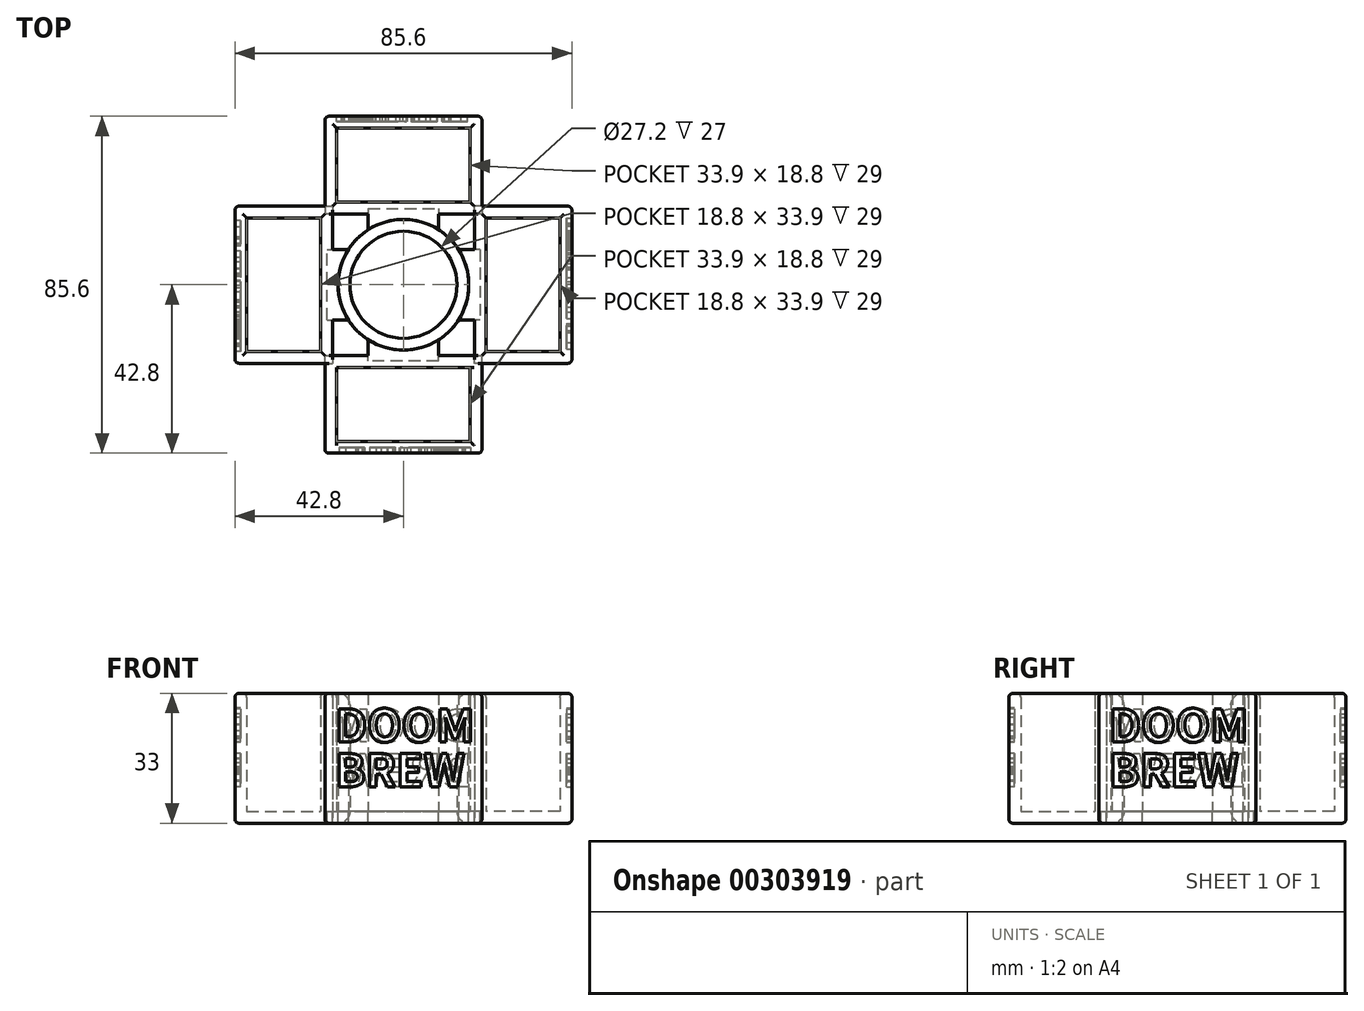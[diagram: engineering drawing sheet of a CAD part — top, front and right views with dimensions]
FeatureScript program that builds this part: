
annotation { "Feature Type Name" : "Feature", "Feature Type Description" : "" }
export const myFeature = defineFeature(function(context is Context, id is Id, definition is map)
    precondition{}
    {
        {
            var Q0;
            Q0=qCreatedBy(makeId("Top.planeOp"),FACE);
            var sketch = newSketch(context, id + "F0", { "sketchPlane" : qUnion([Q0])});
            skLineSegment(sketch, "E0.bottom", {"start": v(16.95, -9.4) * mm, "end": v(-16.95, -9.4) * mm});
            skLineSegment(sketch, "E0.top", {"start": v(16.95, 9.4) * mm, "end": v(-16.95, 9.4) * mm});
            skLineSegment(sketch, "E0.left", {"start": v(16.95, -9.4) * mm, "end": v(16.95, 9.4) * mm});
            skLineSegment(sketch, "E0.right", {"start": v(-16.95, -9.4) * mm, "end": v(-16.95, 9.4) * mm});
            skPoint(sketch, "E0.middle", {"position": v(0, 0) * mm});
            skLineSegment(sketch, "E1.0", {"start": v(19.95, 12.4) * mm, "end": v(-19.95, 12.4) * mm});
            skLineSegment(sketch, "E1.1", {"start": v(19.95, -12.4) * mm, "end": v(19.95, 12.4) * mm});
            skLineSegment(sketch, "E1.2", {"start": v(19.95, -12.4) * mm, "end": v(-19.95, -12.4) * mm});
            skLineSegment(sketch, "E1.3", {"start": v(-19.95, -12.4) * mm, "end": v(-19.95, 12.4) * mm});
            skLineSegment(sketch, "E2", {"start": v(0, 12.4) * mm, "end": v(0, 30.4) * mm, "construction": true});
            skCircle(sketch, "E3", {"center": v(0, 30.4) * mm, "radius": 13.6 * mm});
            skCircle(sketch, "E4.0", {"center": v(0, 30.4) * mm, "radius": 16.6 * mm});
            skLineSegment(sketch, "E5.bottom", {"start": v(8.92, 10.98) * mm, "end": v(-8.92, 10.98) * mm});
            skLineSegment(sketch, "E5.top", {"start": v(8.92, 16.62) * mm, "end": v(-8.92, 16.62) * mm});
            skLineSegment(sketch, "E5.left", {"start": v(8.92, 10.98) * mm, "end": v(8.92, 16.62) * mm});
            skLineSegment(sketch, "E5.right", {"start": v(-8.92, 10.98) * mm, "end": v(-8.92, 16.62) * mm});
            skPoint(sketch, "E5.middle", {"position": v(0, 13.8) * mm});
            skSolve(sketch);
        }
        {
            var Q0;
            Q0=makeQuery(id+"F0.imprint","IMPRINT",FACE,{"disambiguationData":[TD([[makeQuery(id+"F0.imprint","IMPRINT",EDGE,{"derivedFrom":sQuery(id+"F0.wireOp",EDGE,"E0.bottom")}),1.0]])]});
            var Q1;
            {var subQ0=sQuery(id+"F0.wireOp",EDGE,"E1.0");var subQ1=makeQuery(id+"F0.imprint","INTERSECT",VERTEX,{"derivedFrom":[subQ0,sQuery(id+"F0.wireOp",EDGE,"icXzgRXt-Ih2i-wxRq-pmOV-9hTM5KUKghl6")]});Q1=makeQuery(id+"F0.imprint","IMPRINT",FACE,{"disambiguationData":[TD([[makeQuery(id+"F0.imprint","IMPRINT",EDGE,{"disambiguationData":[TD([[subQ1,1.0]])],"derivedFrom":subQ0}),1.0]])]});}
            var Q2;
            {var subQ5=sQuery(id+"F0.wireOp",EDGE,"E5.bottom");Q2=makeQuery(id+"F0.imprint","IMPRINT",FACE,{"disambiguationData":[TD([[makeQuery(id+"F0.imprint","IMPRINT",EDGE,{"derivedFrom":subQ5}),-1.0]])]});}
            var Q3;
            {var subQ0=sQuery(id+"F0.wireOp",EDGE,"E5.left");var subQ1=sQuery(id+"F0.wireOp",EDGE,"E1.0");var subQ2=makeQuery(id+"F0.imprint","INTERSECT",VERTEX,{"derivedFrom":[subQ1,subQ0]});Q3=makeQuery(id+"F0.imprint","IMPRINT",FACE,{"disambiguationData":[TD([[makeQuery(id+"F0.imprint","IMPRINT",EDGE,{"disambiguationData":[TD([[subQ2,-1.0]])],"derivedFrom":subQ1}),-1.0]])]});}
            extrude(context, id + "F1", {"entities" : qUnion([Q0, Q1, Q2, Q3]), "depth" : 30 * mm});
        }
        {
            var Q0;
            Q0=makeQuery(id+"F0.imprint","IMPRINT",FACE,{"disambiguationData":[TD([[makeQuery(id+"F0.imprint","IMPRINT",EDGE,{"derivedFrom":sQuery(id+"F0.wireOp",EDGE,"E0.bottom")}),1.0]])]});
            var Q1;
            {var subQ0=sQuery(id+"F0.wireOp",EDGE,"Or8qQWFx-MEau-wVHM-B5Wl-hgzWRqUUP7mJ");Q1=makeQuery(id+"F0.imprint","IMPRINT",FACE,{"disambiguationData":[TD([[makeQuery(id+"F0.imprint","IMPRINT",EDGE,{"derivedFrom":subQ0}),-1.0]])]});}
            var Q2;
            {var subQ3=sQuery(id+"F0.wireOp",EDGE,"icXzgRXt-Ih2i-wxRq-pmOV-9hTM5KUKghl6");Q2=makeQuery(id+"F0.imprint","IMPRINT",FACE,{"disambiguationData":[TD([[makeQuery(id+"F0.imprint","IMPRINT",EDGE,{"derivedFrom":subQ3}),-1.0]])]});}
            var Q3;
            {var subQ0=sQuery(id+"F0.wireOp",EDGE,"E1.0");var subQ1=makeQuery(id+"F0.imprint","INTERSECT",VERTEX,{"derivedFrom":[subQ0,sQuery(id+"F0.wireOp",EDGE,"icXzgRXt-Ih2i-wxRq-pmOV-9hTM5KUKghl6")]});Q3=makeQuery(id+"F0.imprint","IMPRINT",FACE,{"disambiguationData":[TD([[makeQuery(id+"F0.imprint","IMPRINT",EDGE,{"disambiguationData":[TD([[subQ1,1.0]])],"derivedFrom":subQ0}),1.0]])]});}
            var Q4;
            {var subQ0=sQuery(id+"F0.wireOp",EDGE,"e3ElfhhZ-ileM-0cgF-CI4W-wu8BN25BOuYm");Q4=makeQuery(id+"F0.imprint","IMPRINT",FACE,{"disambiguationData":[TD([[makeQuery(id+"F0.imprint","IMPRINT",EDGE,{"derivedFrom":subQ0}),-1.0]])]});}
            var Q5;
            Q5=makeQuery(id+"F0.imprint","IMPRINT",FACE,{"disambiguationData":[TD([[makeQuery(id+"F0.imprint","IMPRINT",EDGE,{"derivedFrom":sQuery(id+"F0.wireOp",EDGE,"E0.bottom")}),-1.0]])]});
            extrude(context, id + "F2", {"entities" : qUnion([Q0, Q1, Q2, Q3, Q4, Q5]), "operationType" : NewBodyOperationType.ADD, "oppositeDirection" : true, "depth" : 3 * mm});
        }
        {
            var Q0;
            {var subQ0=sQuery(id+"F0.wireOp",EDGE,"E1.2");Q0=makeQuery(id+"F2.boolean.opBoolean","MERGE",FACE,{"derivedFrom":[makeQuery(id+"F1.opExtrude","SWEPT_FACE",FACE,{"disambiguationData":[OSD([subQ0])]}),makeQuery(id+"F2.opExtrude","SWEPT_FACE",FACE,{"disambiguationData":[OSD([subQ0])]})]});}
            var sketch = newSketch(context, id + "F3", { "sketchPlane" : qUnion([Q0])});
            skText(sketch, "E6", { "text": "DOOM\nBREW", "fontName": "NotoSansCJKsc-Bold.otf"});
            const initialGuessF3  = {"E6": [-0.01737, 0.01765, 1, 0, 0.0082]};
            skSetInitialGuess(sketch, initialGuessF3);
            skSolve(sketch);
        }
        {
            var Q0;
            Q0=qSketchRegion(id+"F3",true);
            extrude(context, id + "F4", {"entities" : qUnion([Q0]), "operationType" : NewBodyOperationType.REMOVE, "oppositeDirection" : true, "depth" : 1 * mm});
        }
        {
            var Q0;
            Q0=qSketchRegion(id+"F3",true);
            extrude(context, id + "F5", {"entities" : qUnion([Q0]), "operationType" : NewBodyOperationType.REMOVE, "oppositeDirection" : true, "depth" : 1.4 * mm});
        }
        {
            var Q0;
            Q0=makeQuery(id+"F1.opExtrude","SWEPT_BODY",BODY,{"disambiguationData":[OSD([sQuery(id+"F0.wireOp",EDGE,"E0.bottom"),sQuery(id+"F0.wireOp",EDGE,"E0.top"),sQuery(id+"F0.wireOp",EDGE,"E0.left"),sQuery(id+"F0.wireOp",EDGE,"E0.right"),sQuery(id+"F0.wireOp",EDGE,"E1.0"),sQuery(id+"F0.wireOp",EDGE,"E1.1"),sQuery(id+"F0.wireOp",EDGE,"E1.2"),sQuery(id+"F0.wireOp",EDGE,"E1.3")])]});
            var Q1;
            Q1=sQuery(id+"F0.wireOp",EDGE,"E3");
            circularPattern(context, id + "F6", {"entities" : qUnion([Q0]), "axis" : qUnion([Q1]), "angle" : 360 * degree, "instanceCount" : 4, "equalSpace" : true});
        }
        {
            var Q0;
            Q0=makeQuery(id+"F0.imprint","IMPRINT",FACE,{"disambiguationData":[TD([[makeQuery(id+"F0.imprint","IMPRINT",EDGE,{"derivedFrom":sQuery(id+"F0.wireOp",EDGE,"E3")}),-1.0]])]});
            var Q1;
            {var subQ5=sQuery(id+"F0.wireOp",EDGE,"E5.top");Q1=makeQuery(id+"F0.imprint","IMPRINT",FACE,{"disambiguationData":[TD([[makeQuery(id+"F0.imprint","IMPRINT",EDGE,{"derivedFrom":subQ5}),1.0]])]});}
            extrude(context, id + "F7", {"entities" : qUnion([Q0, Q1]), "depth" : 30 * mm});
        }
        {
            var Q0;
            Q0=makeQuery(id+"F6.opPattern","COPY",FACE,{"derivedFrom":makeQuery(id+"F1.opExtrude","CAP_FACE",FACE,{"disambiguationData":[OSD([sQuery(id+"F0.wireOp",EDGE,"E0.bottom"),sQuery(id+"F0.wireOp",EDGE,"E0.top"),sQuery(id+"F0.wireOp",EDGE,"E0.left"),sQuery(id+"F0.wireOp",EDGE,"E0.right"),sQuery(id+"F0.wireOp",EDGE,"E1.0"),sQuery(id+"F0.wireOp",EDGE,"E1.1"),sQuery(id+"F0.wireOp",EDGE,"E1.2"),sQuery(id+"F0.wireOp",EDGE,"E1.3"),sQuery(id+"F0.wireOp",EDGE,"E4.0"),sQuery(id+"F0.wireOp",EDGE,"E5.left"),sQuery(id+"F0.wireOp",EDGE,"E5.right")])],"isStart":true}),"instanceName":"3"});
            var Q1;
            Q1=makeQuery(id+"F6.opPattern","COPY",FACE,{"derivedFrom":makeQuery(id+"F1.opExtrude","CAP_FACE",FACE,{"disambiguationData":[OSD([sQuery(id+"F0.wireOp",EDGE,"E0.bottom"),sQuery(id+"F0.wireOp",EDGE,"E0.top"),sQuery(id+"F0.wireOp",EDGE,"E0.left"),sQuery(id+"F0.wireOp",EDGE,"E0.right"),sQuery(id+"F0.wireOp",EDGE,"E1.0"),sQuery(id+"F0.wireOp",EDGE,"E1.1"),sQuery(id+"F0.wireOp",EDGE,"E1.2"),sQuery(id+"F0.wireOp",EDGE,"E1.3"),sQuery(id+"F0.wireOp",EDGE,"E4.0"),sQuery(id+"F0.wireOp",EDGE,"E5.left"),sQuery(id+"F0.wireOp",EDGE,"E5.right")])],"isStart":true}),"instanceName":"2"});
            var Q2;
            Q2=makeQuery(id+"F0.imprint","IMPRINT",FACE,{"disambiguationData":[TD([[makeQuery(id+"F0.imprint","IMPRINT",EDGE,{"derivedFrom":sQuery(id+"F0.wireOp",EDGE,"E3")}),-1.0]])]});
            var Q3;
            Q3=makeQuery(id+"F6.opPattern","COPY",FACE,{"derivedFrom":makeQuery(id+"F1.opExtrude","CAP_FACE",FACE,{"disambiguationData":[OSD([sQuery(id+"F0.wireOp",EDGE,"E0.bottom"),sQuery(id+"F0.wireOp",EDGE,"E0.top"),sQuery(id+"F0.wireOp",EDGE,"E0.left"),sQuery(id+"F0.wireOp",EDGE,"E0.right"),sQuery(id+"F0.wireOp",EDGE,"E1.0"),sQuery(id+"F0.wireOp",EDGE,"E1.1"),sQuery(id+"F0.wireOp",EDGE,"E1.2"),sQuery(id+"F0.wireOp",EDGE,"E1.3"),sQuery(id+"F0.wireOp",EDGE,"E4.0"),sQuery(id+"F0.wireOp",EDGE,"E5.left"),sQuery(id+"F0.wireOp",EDGE,"E5.right")])],"isStart":true}),"instanceName":"1"});
            var Q4;
            {var subQ0=sQuery(id+"F0.wireOp",EDGE,"E5.left");var subQ1=sQuery(id+"F0.wireOp",EDGE,"E1.0");var subQ2=makeQuery(id+"F0.imprint","INTERSECT",VERTEX,{"derivedFrom":[subQ1,subQ0]});Q4=makeQuery(id+"F0.imprint","IMPRINT",FACE,{"disambiguationData":[TD([[makeQuery(id+"F0.imprint","IMPRINT",EDGE,{"disambiguationData":[TD([[subQ2,-1.0]])],"derivedFrom":subQ1}),-1.0]])]});}
            var Q5;
            {var subQ5=sQuery(id+"F0.wireOp",EDGE,"E5.bottom");Q5=makeQuery(id+"F0.imprint","IMPRINT",FACE,{"disambiguationData":[TD([[makeQuery(id+"F0.imprint","IMPRINT",EDGE,{"derivedFrom":subQ5}),-1.0]])]});}
            var Q6;
            {var subQ5=sQuery(id+"F0.wireOp",EDGE,"E5.top");Q6=makeQuery(id+"F0.imprint","IMPRINT",FACE,{"disambiguationData":[TD([[makeQuery(id+"F0.imprint","IMPRINT",EDGE,{"derivedFrom":subQ5}),1.0]])]});}
            extrude(context, id + "F8", {"entities" : qUnion([Q0, Q1, Q2, Q3, Q4, Q5, Q6]), "depth" : 3 * mm});
        }
        {
            var Q0;
            Q0=makeQuery(id+"F1.opExtrude","CAP_EDGE",EDGE,{"disambiguationData":[OSD([sQuery(id+"F0.wireOp",EDGE,"E0.bottom")])],"isStart":false});
            var Q1;
            Q1=makeQuery(id+"F1.opExtrude","CAP_EDGE",EDGE,{"disambiguationData":[OSD([sQuery(id+"F0.wireOp",EDGE,"E0.left")])],"isStart":false});
            var Q2;
            Q2=makeQuery(id+"F6.opPattern","COPY",EDGE,{"derivedFrom":makeQuery(id+"F1.opExtrude","CAP_EDGE",EDGE,{"disambiguationData":[OSD([sQuery(id+"F0.wireOp",EDGE,"E0.right")])],"isStart":false}),"instanceName":"1"});
            var Q3;
            Q3=makeQuery(id+"F6.opPattern","COPY",EDGE,{"derivedFrom":makeQuery(id+"F1.opExtrude","CAP_EDGE",EDGE,{"disambiguationData":[OSD([sQuery(id+"F0.wireOp",EDGE,"E0.bottom")])],"isStart":false}),"instanceName":"1"});
            var Q4;
            Q4=makeQuery(id+"F6.opPattern","COPY",EDGE,{"derivedFrom":makeQuery(id+"F1.opExtrude","CAP_EDGE",EDGE,{"disambiguationData":[OSD([sQuery(id+"F0.wireOp",EDGE,"E0.left")])],"isStart":false}),"instanceName":"1"});
            var Q5;
            Q5=makeQuery(id+"F6.opPattern","COPY",EDGE,{"derivedFrom":makeQuery(id+"F1.opExtrude","CAP_EDGE",EDGE,{"disambiguationData":[OSD([sQuery(id+"F0.wireOp",EDGE,"E0.top")])],"isStart":false}),"instanceName":"1"});
            var Q6;
            Q6=makeQuery(id+"F6.opPattern","COPY",EDGE,{"derivedFrom":makeQuery(id+"F1.opExtrude","CAP_EDGE",EDGE,{"disambiguationData":[OSD([sQuery(id+"F0.wireOp",EDGE,"E0.top")])],"isStart":false}),"instanceName":"3"});
            var Q7;
            Q7=makeQuery(id+"F6.opPattern","COPY",EDGE,{"derivedFrom":makeQuery(id+"F1.opExtrude","CAP_EDGE",EDGE,{"disambiguationData":[OSD([sQuery(id+"F0.wireOp",EDGE,"E0.left")])],"isStart":false}),"instanceName":"3"});
            var Q8;
            Q8=makeQuery(id+"F6.opPattern","COPY",EDGE,{"derivedFrom":makeQuery(id+"F1.opExtrude","CAP_EDGE",EDGE,{"disambiguationData":[OSD([sQuery(id+"F0.wireOp",EDGE,"E1.1")])],"isStart":false}),"instanceName":"3"});
            var Q9;
            Q9=makeQuery(id+"F1.opExtrude","CAP_EDGE",EDGE,{"disambiguationData":[OSD([sQuery(id+"F0.wireOp",EDGE,"E1.3")])],"isStart":false});
            var Q10;
            Q10=makeQuery(id+"F1.opExtrude","CAP_EDGE",EDGE,{"disambiguationData":[OSD([sQuery(id+"F0.wireOp",EDGE,"E1.2")])],"isStart":false});
            var Q11;
            Q11=makeQuery(id+"F1.opExtrude","CAP_EDGE",EDGE,{"disambiguationData":[OSD([sQuery(id+"F0.wireOp",EDGE,"E1.1")])],"isStart":false});
            var Q12;
            Q12=makeQuery(id+"F6.opPattern","COPY",EDGE,{"derivedFrom":makeQuery(id+"F1.opExtrude","CAP_EDGE",EDGE,{"disambiguationData":[OSD([sQuery(id+"F0.wireOp",EDGE,"E0.bottom")])],"isStart":false}),"instanceName":"3"});
            var Q13;
            Q13=makeQuery(id+"F6.opPattern","COPY",EDGE,{"derivedFrom":makeQuery(id+"F1.opExtrude","CAP_EDGE",EDGE,{"disambiguationData":[OSD([sQuery(id+"F0.wireOp",EDGE,"E0.right")])],"isStart":false}),"instanceName":"3"});
            var Q14;
            Q14=makeQuery(id+"F6.opPattern","COPY",EDGE,{"derivedFrom":makeQuery(id+"F1.opExtrude","CAP_EDGE",EDGE,{"disambiguationData":[OSD([sQuery(id+"F0.wireOp",EDGE,"E1.3")])],"isStart":false}),"instanceName":"3"});
            var Q15;
            Q15=makeQuery(id+"F6.opPattern","COPY",EDGE,{"derivedFrom":makeQuery(id+"F1.opExtrude","CAP_EDGE",EDGE,{"disambiguationData":[OSD([sQuery(id+"F0.wireOp",EDGE,"E1.2")])],"isStart":false}),"instanceName":"3"});
            var Q16;
            Q16=makeQuery(id+"F6.opPattern","COPY",EDGE,{"derivedFrom":makeQuery(id+"F1.opExtrude","CAP_EDGE",EDGE,{"disambiguationData":[OSD([sQuery(id+"F0.wireOp",EDGE,"E0.left")])],"isStart":false}),"instanceName":"2"});
            var Q17;
            Q17=makeQuery(id+"F6.opPattern","COPY",EDGE,{"derivedFrom":makeQuery(id+"F1.opExtrude","CAP_EDGE",EDGE,{"disambiguationData":[OSD([sQuery(id+"F0.wireOp",EDGE,"E1.1")])],"isStart":false}),"instanceName":"2"});
            var Q18;
            Q18=makeQuery(id+"F6.opPattern","COPY",EDGE,{"derivedFrom":makeQuery(id+"F1.opExtrude","CAP_EDGE",EDGE,{"disambiguationData":[OSD([sQuery(id+"F0.wireOp",EDGE,"E1.2")])],"isStart":false}),"instanceName":"2"});
            var Q19;
            Q19=makeQuery(id+"F6.opPattern","COPY",EDGE,{"derivedFrom":makeQuery(id+"F1.opExtrude","CAP_EDGE",EDGE,{"disambiguationData":[OSD([sQuery(id+"F0.wireOp",EDGE,"E0.bottom")])],"isStart":false}),"instanceName":"2"});
            var Q20;
            Q20=makeQuery(id+"F6.opPattern","COPY",EDGE,{"derivedFrom":makeQuery(id+"F1.opExtrude","CAP_EDGE",EDGE,{"disambiguationData":[OSD([sQuery(id+"F0.wireOp",EDGE,"E0.top")])],"isStart":false}),"instanceName":"2"});
            var Q21;
            Q21=makeQuery(id+"F6.opPattern","COPY",EDGE,{"derivedFrom":makeQuery(id+"F1.opExtrude","CAP_EDGE",EDGE,{"disambiguationData":[OSD([sQuery(id+"F0.wireOp",EDGE,"E0.right")])],"isStart":false}),"instanceName":"2"});
            var Q22;
            Q22=makeQuery(id+"F6.opPattern","COPY",EDGE,{"derivedFrom":makeQuery(id+"F1.opExtrude","CAP_EDGE",EDGE,{"disambiguationData":[OSD([sQuery(id+"F0.wireOp",EDGE,"E1.3")])],"isStart":false}),"instanceName":"2"});
            var Q23;
            Q23=makeQuery(id+"F6.opPattern","COPY",EDGE,{"derivedFrom":makeQuery(id+"F1.opExtrude","CAP_EDGE",EDGE,{"disambiguationData":[OSD([sQuery(id+"F0.wireOp",EDGE,"E1.1")])],"isStart":false}),"instanceName":"1"});
            var Q24;
            Q24=makeQuery(id+"F6.opPattern","COPY",EDGE,{"derivedFrom":makeQuery(id+"F1.opExtrude","CAP_EDGE",EDGE,{"disambiguationData":[OSD([sQuery(id+"F0.wireOp",EDGE,"E1.2")])],"isStart":false}),"instanceName":"1"});
            var Q25;
            {var subQ0=sQuery(id+"F0.wireOp",EDGE,"E1.2");var subQ1=sQuery(id+"F0.wireOp",EDGE,"E1.1");Q25=makeQuery(id+"F6.opPattern","COPY",EDGE,{"derivedFrom":makeQuery(id+"F2.boolean.opBoolean","MERGE",EDGE,{"derivedFrom":[makeQuery(id+"F1.opExtrude","SWEPT_EDGE",EDGE,{"disambiguationData":[OSD([subQ1,subQ0])]}),makeQuery(id+"F2.opExtrude","SWEPT_EDGE",EDGE,{"disambiguationData":[OSD([subQ1,subQ0])]})]}),"instanceName":"1"});}
            var Q26;
            {var subQ0=sQuery(id+"F0.wireOp",EDGE,"E1.3");var subQ1=sQuery(id+"F0.wireOp",EDGE,"E1.2");Q26=makeQuery(id+"F6.opPattern","COPY",EDGE,{"derivedFrom":makeQuery(id+"F2.boolean.opBoolean","MERGE",EDGE,{"derivedFrom":[makeQuery(id+"F1.opExtrude","SWEPT_EDGE",EDGE,{"disambiguationData":[OSD([subQ1,subQ0])]}),makeQuery(id+"F2.opExtrude","SWEPT_EDGE",EDGE,{"disambiguationData":[OSD([subQ1,subQ0])]})]}),"instanceName":"2"});}
            var Q27;
            {var subQ0=sQuery(id+"F0.wireOp",EDGE,"E1.2");var subQ1=sQuery(id+"F0.wireOp",EDGE,"E1.1");Q27=makeQuery(id+"F6.opPattern","COPY",EDGE,{"derivedFrom":makeQuery(id+"F2.boolean.opBoolean","MERGE",EDGE,{"derivedFrom":[makeQuery(id+"F1.opExtrude","SWEPT_EDGE",EDGE,{"disambiguationData":[OSD([subQ1,subQ0])]}),makeQuery(id+"F2.opExtrude","SWEPT_EDGE",EDGE,{"disambiguationData":[OSD([subQ1,subQ0])]})]}),"instanceName":"2"});}
            var Q28;
            {var subQ0=sQuery(id+"F0.wireOp",EDGE,"E1.3");var subQ1=sQuery(id+"F0.wireOp",EDGE,"E1.2");Q28=makeQuery(id+"F6.opPattern","COPY",EDGE,{"derivedFrom":makeQuery(id+"F2.boolean.opBoolean","MERGE",EDGE,{"derivedFrom":[makeQuery(id+"F1.opExtrude","SWEPT_EDGE",EDGE,{"disambiguationData":[OSD([subQ1,subQ0])]}),makeQuery(id+"F2.opExtrude","SWEPT_EDGE",EDGE,{"disambiguationData":[OSD([subQ1,subQ0])]})]}),"instanceName":"3"});}
            var Q29;
            {var subQ0=sQuery(id+"F0.wireOp",EDGE,"E1.2");var subQ1=sQuery(id+"F0.wireOp",EDGE,"E1.1");Q29=makeQuery(id+"F6.opPattern","COPY",EDGE,{"derivedFrom":makeQuery(id+"F2.boolean.opBoolean","MERGE",EDGE,{"derivedFrom":[makeQuery(id+"F1.opExtrude","SWEPT_EDGE",EDGE,{"disambiguationData":[OSD([subQ1,subQ0])]}),makeQuery(id+"F2.opExtrude","SWEPT_EDGE",EDGE,{"disambiguationData":[OSD([subQ1,subQ0])]})]}),"instanceName":"3"});}
            var Q30;
            {var subQ0=sQuery(id+"F0.wireOp",EDGE,"E1.3");var subQ1=sQuery(id+"F0.wireOp",EDGE,"E1.2");Q30=makeQuery(id+"F2.boolean.opBoolean","MERGE",EDGE,{"derivedFrom":[makeQuery(id+"F1.opExtrude","SWEPT_EDGE",EDGE,{"disambiguationData":[OSD([subQ1,subQ0])]}),makeQuery(id+"F2.opExtrude","SWEPT_EDGE",EDGE,{"disambiguationData":[OSD([subQ1,subQ0])]})]});}
            var Q31;
            {var subQ0=sQuery(id+"F0.wireOp",EDGE,"E1.2");var subQ1=sQuery(id+"F0.wireOp",EDGE,"E1.1");Q31=makeQuery(id+"F2.boolean.opBoolean","MERGE",EDGE,{"derivedFrom":[makeQuery(id+"F1.opExtrude","SWEPT_EDGE",EDGE,{"disambiguationData":[OSD([subQ1,subQ0])]}),makeQuery(id+"F2.opExtrude","SWEPT_EDGE",EDGE,{"disambiguationData":[OSD([subQ1,subQ0])]})]});}
            var Q32;
            {var subQ0=sQuery(id+"F0.wireOp",EDGE,"E1.3");var subQ1=sQuery(id+"F0.wireOp",EDGE,"E1.2");Q32=makeQuery(id+"F6.opPattern","COPY",EDGE,{"derivedFrom":makeQuery(id+"F2.boolean.opBoolean","MERGE",EDGE,{"derivedFrom":[makeQuery(id+"F1.opExtrude","SWEPT_EDGE",EDGE,{"disambiguationData":[OSD([subQ1,subQ0])]}),makeQuery(id+"F2.opExtrude","SWEPT_EDGE",EDGE,{"disambiguationData":[OSD([subQ1,subQ0])]})]}),"instanceName":"1"});}
            var Q33;
            Q33=makeQuery(id+"F6.opPattern","COPY",EDGE,{"derivedFrom":makeQuery(id+"F1.opExtrude","CAP_EDGE",EDGE,{"disambiguationData":[OSD([sQuery(id+"F0.wireOp",EDGE,"E1.3")])],"isStart":false}),"instanceName":"1"});
            var Q34;
            Q34=makeQuery(id+"F2.opExtrude","CAP_EDGE",EDGE,{"disambiguationData":[OSD([sQuery(id+"F0.wireOp",EDGE,"E1.2")])],"isStart":false});
            var Q35;
            Q35=makeQuery(id+"F6.opPattern","COPY",EDGE,{"derivedFrom":makeQuery(id+"F2.opExtrude","CAP_EDGE",EDGE,{"disambiguationData":[OSD([sQuery(id+"F0.wireOp",EDGE,"E1.2")])],"isStart":false}),"instanceName":"1"});
            var Q36;
            Q36=makeQuery(id+"F6.opPattern","COPY",EDGE,{"derivedFrom":makeQuery(id+"F2.opExtrude","CAP_EDGE",EDGE,{"disambiguationData":[OSD([sQuery(id+"F0.wireOp",EDGE,"E1.3")])],"isStart":false}),"instanceName":"1"});
            var Q37;
            Q37=makeQuery(id+"F2.opExtrude","CAP_EDGE",EDGE,{"disambiguationData":[OSD([sQuery(id+"F0.wireOp",EDGE,"E1.1")])],"isStart":false});
            var Q38;
            Q38=makeQuery(id+"F2.opExtrude","CAP_EDGE",EDGE,{"disambiguationData":[OSD([sQuery(id+"F0.wireOp",EDGE,"E1.3")])],"isStart":false});
            var Q39;
            Q39=makeQuery(id+"F6.opPattern","COPY",EDGE,{"derivedFrom":makeQuery(id+"F2.opExtrude","CAP_EDGE",EDGE,{"disambiguationData":[OSD([sQuery(id+"F0.wireOp",EDGE,"E1.1")])],"isStart":false}),"instanceName":"3"});
            var Q40;
            Q40=makeQuery(id+"F6.opPattern","COPY",EDGE,{"derivedFrom":makeQuery(id+"F2.opExtrude","CAP_EDGE",EDGE,{"disambiguationData":[OSD([sQuery(id+"F0.wireOp",EDGE,"E1.2")])],"isStart":false}),"instanceName":"3"});
            var Q41;
            Q41=makeQuery(id+"F6.opPattern","COPY",EDGE,{"derivedFrom":makeQuery(id+"F2.opExtrude","CAP_EDGE",EDGE,{"disambiguationData":[OSD([sQuery(id+"F0.wireOp",EDGE,"E1.1")])],"isStart":false}),"instanceName":"2"});
            var Q42;
            Q42=makeQuery(id+"F6.opPattern","COPY",EDGE,{"derivedFrom":makeQuery(id+"F2.opExtrude","CAP_EDGE",EDGE,{"disambiguationData":[OSD([sQuery(id+"F0.wireOp",EDGE,"E1.3")])],"isStart":false}),"instanceName":"3"});
            var Q43;
            Q43=makeQuery(id+"F6.opPattern","COPY",EDGE,{"derivedFrom":makeQuery(id+"F2.opExtrude","CAP_EDGE",EDGE,{"disambiguationData":[OSD([sQuery(id+"F0.wireOp",EDGE,"E1.1")])],"isStart":false}),"instanceName":"1"});
            var Q44;
            Q44=makeQuery(id+"F6.opPattern","COPY",EDGE,{"derivedFrom":makeQuery(id+"F2.opExtrude","CAP_EDGE",EDGE,{"disambiguationData":[OSD([sQuery(id+"F0.wireOp",EDGE,"E1.3")])],"isStart":false}),"instanceName":"2"});
            var Q45;
            Q45=makeQuery(id+"F6.opPattern","COPY",EDGE,{"derivedFrom":makeQuery(id+"F2.opExtrude","CAP_EDGE",EDGE,{"disambiguationData":[OSD([sQuery(id+"F0.wireOp",EDGE,"E1.2")])],"isStart":false}),"instanceName":"2"});
            fillet(context, id + "F9", {"entities" : qUnion([Q0, Q1, Q2, Q3, Q4, Q5, Q6, Q7, Q8, Q9, Q10, Q11, Q12, Q13, Q14, Q15, Q16, Q17, Q18, Q19, Q20, Q21, Q22, Q23, Q24, Q25, Q26, Q27, Q28, Q29, Q30, Q31, Q32, Q33, Q34, Q35, Q36, Q37, Q38, Q39, Q40, Q41, Q42, Q43, Q44, Q45]), "radius" : 1 * mm, "tangentPropagation" : true, "allowEdgeOverflow" : false});
        }
        {
            var Q0;
            Q0=makeQuery(id+"F7.opExtrude","CAP_EDGE",EDGE,{"disambiguationData":[OSD([sQuery(id+"F0.wireOp",EDGE,"E3")])],"isStart":false});
            var Q1;
            Q1=makeQuery(id+"F8.opExtrude","CAP_EDGE",EDGE,{"disambiguationData":[OSD([sQuery(id+"F0.wireOp",EDGE,"E3")])],"isStart":false});
            fillet(context, id + "F10", {"entities" : qUnion([Q0, Q1]), "radius" : 3 * mm, "tangentPropagation" : true, "allowEdgeOverflow" : false});
        }
    });
